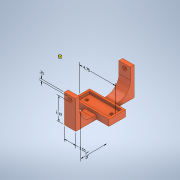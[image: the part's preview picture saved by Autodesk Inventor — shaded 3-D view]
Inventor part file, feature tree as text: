
AUTODESK INVENTOR PART (.ipt)
format: ipt  version: 2022 (Build 260153070, 153G)  size: 1,933,312 bytes
history: native  units: in
note: dims shown in document units (in); Inventor stores cm internally (conversion verified against a paired STEP export)
features: other x6, sketch x6, extrude x6, hole x1, mirror x1, fillet x1
ambient origin geometry x8: Origin, YZ Plane, XZ Plane, XY Plane, X Axis, Y Axis, Z Axis, Center Point
bodies: Solid1 (feature_tree)
feature tree (21):
  other  "Annotations"
  sketch  "Sketch1"  dims[d0=1.7in d1=4.25in]
  extrude  "Extrusion1"  Depth=4.25in
  extrude  "Extrusion2"  Depth=0.25in
  hole  "Hole1"  [1 undecoded]
  extrude  "Extrusion10"  TaperAngle=0.0deg  [1 undecoded]
  extrude  "Extrusion11"  Depth=0.5in
  extrude  "Extrusion12"  Depth=0.05in
  mirror  "Mirror8"
  fillet  "Fillet1"  Radius=0.375in
  extrude  "Extrusion13"  Depth=0.05in TaperAngle=0.0deg
  sketch  "Sketch2"  dims[d2=0.25in d3=0.25in]
  sketch  "Sketch15"  dims[d4=0.475in d5=0.0in]
  sketch  "Sketch16"  dims[d6=0.35in d7=0.0in]
  sketch  "Sketch17"  dims[d8=0.5in d9=0.5in]
  sketch  "Sketch18"  dims[d10=0.201in d11=0.75in d12=0.4in d13=0.1in d14=0.5635in d15=1.0in d16=0.8108in d17=0.375in d24=0.375in d101=2.75in d102=0.0in d103=0.5in d104=3.25in d105=0.0in d109=1.5in d115=0.0in d116=0.0in d117=1.75in d119=0.5in d120=0.51in d140=0.05in d141=0.0in d106=0.9428in d107=4.2237in d108=3.35in d110=0.3497in d111=0.335in d112=1.5in d125=0.0966in d126=0.3041in d127=2.97in d128=0.1855in d129=0.2047in d130=0.245in d92=0.237in d93=0.16in d94=4.75in d121=0.5in d122=0.0344in]
  other  "Linear Dimension 1"
  other  "Linear Dimension 4"
  other  "Linear Dimension 5"
  other  "Linear Dimension 6"
  other  "Linear Dimension 7"
note: 2 required parameter values undecoded (feature->parameter linkage not recoverable at this tier; creation-order binding heuristic only, values carry confidence <= 0.55)
